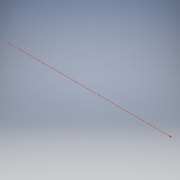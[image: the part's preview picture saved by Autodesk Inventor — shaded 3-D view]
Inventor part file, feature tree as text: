
AUTODESK INVENTOR PART (.ipt)
format: ipt  version: 2016 (Build 200138000, 138)  size: 92,672 bytes
history: native  units: mm
features: sketch x2, extrude x1, revolve x1
ambient origin geometry x8: Origin, YZ Plane, XZ Plane, XY Plane, X Axis, Y Axis, Z Axis, Center Point
bodies: Solid1 (feature_tree)
feature tree (4):
  extrude  "Extrusion1"  Depth=3000.0mm TaperAngle=0.0deg
  revolve  "Revolution1"  Angle=90.0deg
  sketch  "Sketch1"  dims[d0=5.0mm d1=3000.0mm d2=0.0mm]
  sketch  "Sketch2"  dims[d3=25.0mm d4=90.0deg d5=0.0mm]
